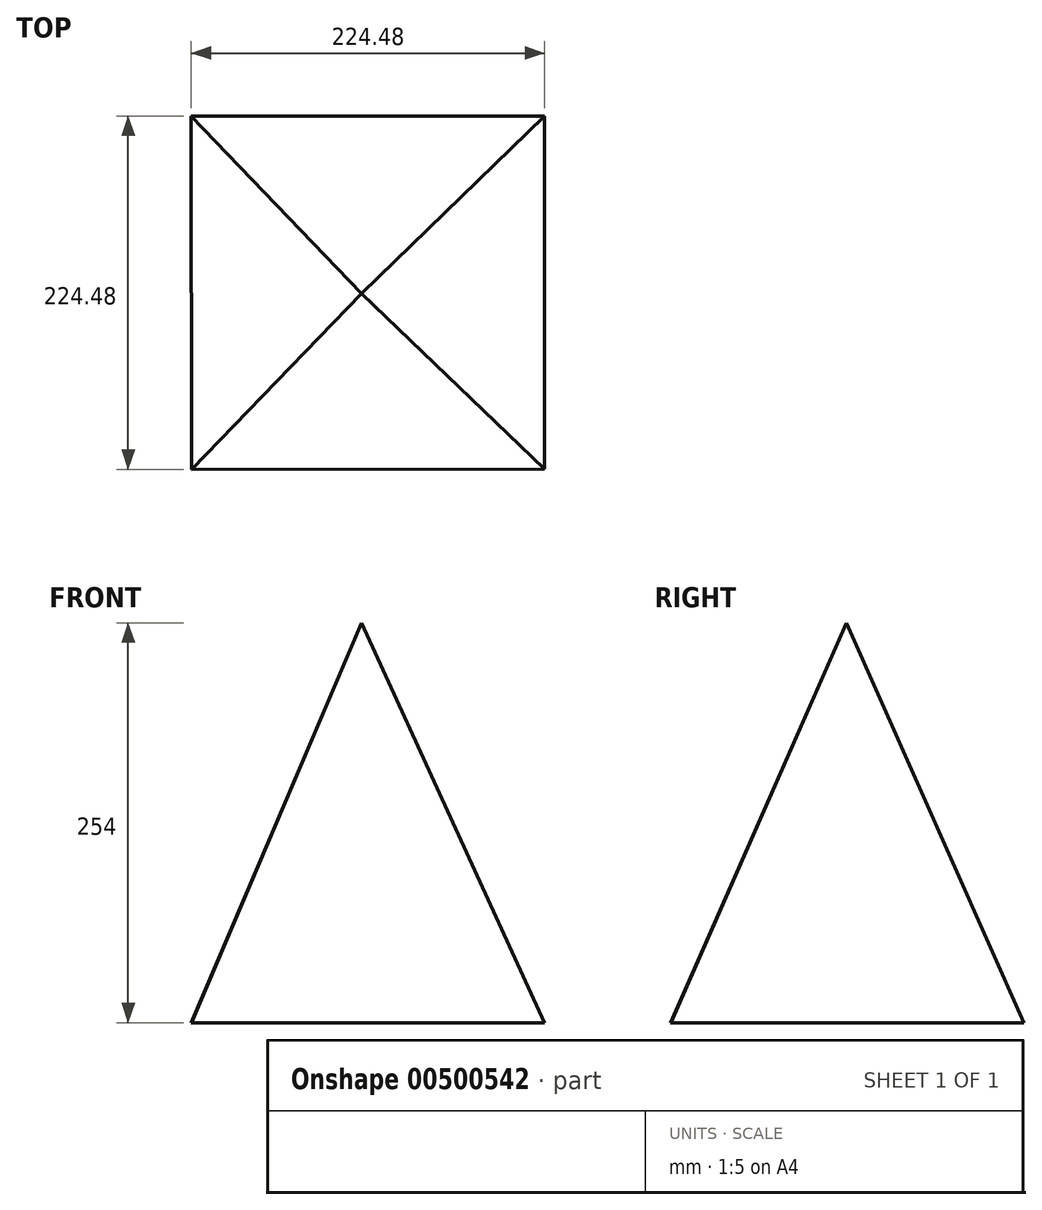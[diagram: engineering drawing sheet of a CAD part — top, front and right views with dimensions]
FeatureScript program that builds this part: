
annotation { "Feature Type Name" : "Feature", "Feature Type Description" : "" }
export const myFeature = defineFeature(function(context is Context, id is Id, definition is map)
    precondition{}
    {
        {
            var Q0;
            Q0=qCreatedBy(makeId("Top.planeOp"),FACE);
            var sketch = newSketch(context, id + "F0", { "sketchPlane" : qUnion([Q0])});
            skCircle(sketch, "E0.cCircle", {"center": v(0, 0) * mm, "radius": 158.52 * mm, "construction": true});
            skLineSegment(sketch, "E0.0", {"start": v(-112.24, 111.94) * mm, "end": v(111.94, 112.24) * mm});
            skLineSegment(sketch, "E0.1", {"start": v(111.94, 112.24) * mm, "end": v(112.24, -111.94) * mm});
            skLineSegment(sketch, "E0.2", {"start": v(112.24, -111.94) * mm, "end": v(-111.94, -112.24) * mm});
            skLineSegment(sketch, "E0.3", {"start": v(-111.94, -112.24) * mm, "end": v(-112.24, 111.94) * mm});
            skSolve(sketch);
        }
        {
            var Q0;
            Q0=qCreatedBy(makeId("Top.planeOp"),FACE);
            cPlane(context, id + "F1", {"entities" : qUnion([Q0]), "cplaneType" : CPlaneType.OFFSET, "offset" : 254 * mm, "width" : 152.4 * mm, "height" : 152.4 * mm});
        }
        {
            var Q0;
            Q0=qCreatedBy(id+"F1.planeOp",FACE);
            var sketch = newSketch(context, id + "F2", { "sketchPlane" : qUnion([Q0])});
            skPoint(sketch, "E1", {"position": v(-4.02, -0.63) * mm});
            skSolve(sketch);
        }
        {
            var Q0;
            Q0=sQuery(id+"F2.wireOp",VERTEX,"E1");
            var Q1;
            Q1=makeQuery(id+"F0.imprint","IMPRINT",FACE,{"disambiguationData":[TD([[makeQuery(id+"F0.imprint","IMPRINT",EDGE,{"derivedFrom":sQuery(id+"F0.wireOp",EDGE,"E0.0")}),-1.0]])]});
            loft(context, id + "F3", {"sheetProfilesArray" : [{ "sheetProfileEntities" : qUnion([Q0]) }, { "sheetProfileEntities" : qUnion([Q1]) }]});
        }
    });
